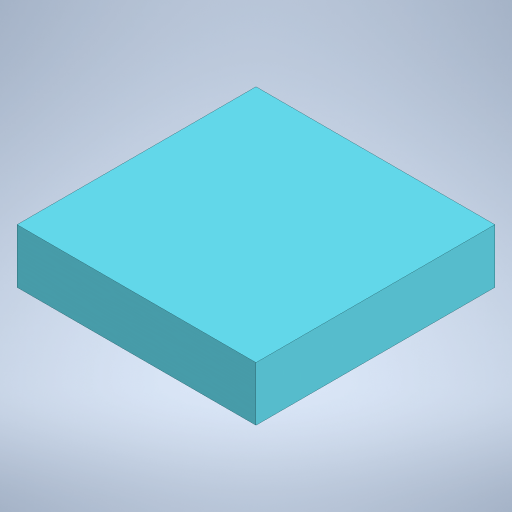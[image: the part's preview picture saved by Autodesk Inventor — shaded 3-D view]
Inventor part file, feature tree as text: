
AUTODESK INVENTOR PART (.ipt)
format: ipt  version: 2024 (Build 280153000, 153)  size: 5,346,304 bytes
history: native  units: mm
features: other x26, surface_op x18, fillet x9, sketch x9, extrude x6, revolve x4, plane x3, pattern_circular x2, loft x1
ambient origin geometry x8: Origin, YZ Plane, XZ Plane, XY Plane, X Axis, Y Axis, Z Axis, Center Point
bodies: Body1 (feature_tree), Body2 (feature_tree), Body3 (feature_tree), Body4 (feature_tree), Body5 (feature_tree), Body6 (feature_tree), Body7 (feature_tree), Body8 (feature_tree), Body9 (feature_tree), Body10 (feature_tree), Body11 (feature_tree), Body12 (feature_tree), Body13 (feature_tree), Body14 (feature_tree), Body15 (feature_tree), Body16 (feature_tree), Body17 (feature_tree), Body18 (feature_tree), Body19 (feature_tree), Body20 (feature_tree), Body21 (feature_tree), Body22 (feature_tree), Body23 (feature_tree), Body24 (feature_tree), Body25 (feature_tree), Body26 (feature_tree), Body27 (feature_tree)
feature tree (78):
  plane  "Work Plane1"
  plane  "Work Plane4"
  plane  "Work Plane5"
  surface_op  "Trim1"
  surface_op  "Trim2"
  surface_op  "Trim3"
  surface_op  "Trim4"
  fillet  "Fillet1"  Radius=200.0mm
  pattern_circular  "Circular Pattern1"  Count=11  [1 undecoded]
  surface_op  "Stitch Surface2"
  pattern_circular  "Circular Pattern3"  Count=3  [1 undecoded]
  surface_op  "Trim7"
  surface_op  "Trim8"
  surface_op  "Trim9"
  surface_op  "Trim10"
  surface_op  "Trim11"
  surface_op  "Stitch Surface3"
  extrude  "Extrusion4"  Depth=200.0mm
  surface_op  "Sculpt2"
  sketch  "Sketch1"  dims[d2=463.0mm]
  other  "Srf1"
  sketch  "Sketch2"  dims[d3=138.0mm]
  other  "Srf2"
  sketch  "Sketch3"  dims[d4=95.0mm]
  other  "Srf3"
  sketch  "Sketch4"  dims[d5=84.0mm]
  sketch  "Sketch7"  dims[d6=33.0mm]
  sketch  "Sketch8"  dims[d7=12.566371mm d8=30.0mm]
  other  "Srf4"
  other  "Srf5"
  other  "Srf6"
  sketch  "Sketch9"  dims[d9=35.0mm d10=200.0mm]
  other  "Srf7"
  other  "Srf8"
  other  "Srf9"
  other  "Srf10"
  other  "Srf11"
  other  "Srf12"
  other  "Srf13"
  other  "Srf15"
  sketch  "Sketch11"  dims[d11=12.566371mm d12=369.0mm]
  other  "Srf18"
  other  "Srf19"
  other  "Srf20"
  other  "Srf21"
  other  "Srf22"
  other  "Srf23"
  other  "Srf24"
  other  "Srf25"
  other  "Srf26"
  other  "Srf27"
  other  "Srf29"
  other  "Srf30"
  sketch  "Sketch13"  dims[d13=50.0mm d14=245.0mm d15=16.0mm d16=130.0mm d17=63.0mm d18=12.566371mm d19=120.0mm d21=-25.0mm d22=-120.0mm d27=100.0mm d28=152.0mm d29=80.0mm d30=45.0mm d31=6.283185mm d32=6.283185mm d33=360.0mm d36=25.0mm d37=50.0mm d38=0.0mm d39=90.0deg d40=0.0mm d41=90.0deg d42=0.0mm d43=90.0deg d44=15.0mm d45=25.0mm d46=30.0mm d47=30.0mm d48=70.0mm d49=80.0mm d50=20.0mm d51=75.0mm d52=12.566371mm d53=5.0mm d54=5.0mm d55=5.0mm d56=5.0mm d57=5.0mm d58=5.0mm d59=5.0mm d60=5.0mm d61=50.0mm d62=360.0deg d68=80.0mm d69=300.0mm d79=10.0mm d80=0.0mm d81=50.0mm d82=360.0deg d84=5.0mm d85=0.0mm d86=5.0mm d87=0.0mm d88=5.0mm d89=0.0mm d90=5.0mm d91=0.0mm d92=5.0mm d93=0.0mm d102=5.0mm d103=0.0mm d104=1100.0mm d105=550.0mm d106=250.0mm d107=68.0mm d108=1100.0mm d109=0.0mm]
  revolve  "RevolutionSrf1"  [1 undecoded]
  revolve  "RevolutionSrf2"  [1 undecoded]
  revolve  "RevolutionSrf3"  [1 undecoded]
  loft  "LoftSrf1"
  fillet  "Face Fillet2"
  revolve  "RevolutionSrf4"  [1 undecoded]
  fillet  "Face Fillet4"
  extrude  "ExtrusionSrf3"  Depth=12.566371mm
  fillet  "Face Fillet1"
  fillet  "Face Fillet3"
  fillet  "Face Fillet5"
  fillet  "Face Fillet6"
  fillet  "Face Fillet7"
  fillet  "Face Fillet8"
  extrude  "ExtrusionSrf4"  Depth=120.0mm
  extrude  "ExtrusionSrf5"  Depth=100.0mm
  extrude  "ExtrusionSrf6"  Depth=152.0mm
  extrude  "ExtrusionSrf7"  Depth=80.0mm
  surface_op  "Boundary Patch1"
  surface_op  "Boundary Patch2"
  surface_op  "Boundary Patch3"
  surface_op  "Boundary Patch4"
  surface_op  "Boundary Patch5"
  surface_op  "Boundary Patch7"
note: 6 required parameter values undecoded (feature->parameter linkage not recoverable at this tier; creation-order binding heuristic only, values carry confidence <= 0.55)